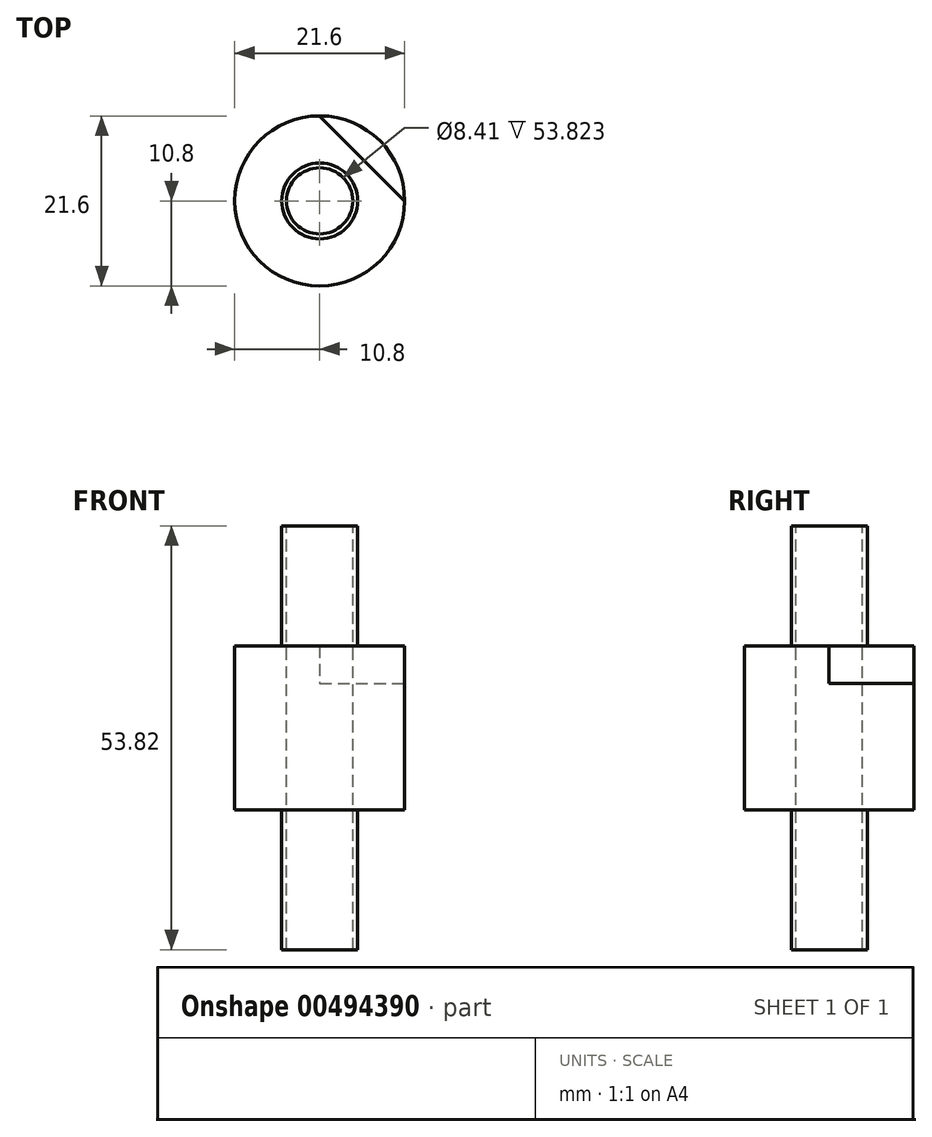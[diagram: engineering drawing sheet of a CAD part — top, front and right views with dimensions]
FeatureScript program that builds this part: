
annotation { "Feature Type Name" : "Feature", "Feature Type Description" : "" }
export const myFeature = defineFeature(function(context is Context, id is Id, definition is map)
    precondition{}
    {
        {
            var Q0;
            Q0=qCreatedBy(makeId("Front.planeOp"),FACE);
            var sketch = newSketch(context, id + "F0", { "sketchPlane" : qUnion([Q0])});
            skLineSegment(sketch, "E0", {"start": v(0, 19.99) * mm, "end": v(-4.83, 19.99) * mm});
            skLineSegment(sketch, "E1", {"start": v(-4.83, 19.99) * mm, "end": v(-4.83, 0) * mm});
            skLineSegment(sketch, "E2", {"start": v(-4.83, 0) * mm, "end": v(-10.8, 0) * mm});
            skLineSegment(sketch, "E3", {"start": v(-10.8, 0) * mm, "end": v(-10.8, -16.05) * mm});
            skLineSegment(sketch, "E4", {"start": v(-10.8, -16.05) * mm, "end": v(-4.83, -16.05) * mm});
            skLineSegment(sketch, "E5", {"start": v(-4.83, -16.05) * mm, "end": v(-4.83, -33.83) * mm});
            skLineSegment(sketch, "E6", {"start": v(-4.83, -33.83) * mm, "end": v(0, -33.83) * mm});
            skLineSegment(sketch, "E7", {"start": v(0, -33.83) * mm, "end": v(0, 19.99) * mm});
            skSolve(sketch);
        }
        {
            var Q0;
            Q0 = qSketchRegion(id + "F0", true);
            var Q1;
            Q1=sQuery(id+"F0.wireOp",EDGE,"E7");
            revolve(context, id + "F1", {"entities" : qUnion([Q0]), "axis" : qUnion([Q1]), "revolveType" : RevolveType.FULL});
        }
        {
            var Q0;
            Q0=makeQuery(id+"F1.opRevolve","SWEPT_FACE",FACE,{"disambiguationData":[OSD([sQuery(id+"F0.wireOp",EDGE,"E2")])]});
            var sketch = newSketch(context, id + "F2", { "sketchPlane" : qUnion([Q0])});
            skArc(sketch, "E8", {"start": v(0, 10.8) * mm, "mid": v(-7.63, -7.63) * mm, "end": v(10.8, 0) * mm});
            skLineSegment(sketch, "E9", {"start": v(0, 10.8) * mm, "end": v(10.8, 0) * mm});
            skSolve(sketch);
        }
        {
            var Q0;
            Q0 = qSketchRegion(id + "F2", true);
            extrude(context, id + "F3", {"entities" : qUnion([Q0]), "operationType" : NewBodyOperationType.ADD, "depth" : 4.75 * mm});
        }
        {
            var Q0;
            Q0=makeQuery(id+"F1.opRevolve","SWEPT_FACE",FACE,{"disambiguationData":[OSD([sQuery(id+"F0.wireOp",EDGE,"E0")])]});
            var sketch = newSketch(context, id + "F4", { "sketchPlane" : qUnion([Q0])});
            skCircle(sketch, "E10", {"center": v(0, 0) * mm, "radius": 4.2 * mm});
            skSolve(sketch);
        }
        {
            var Q0;
            Q0=sQuery(id+"F4.wireOp",VERTEX,"E10.center");
            var Q1;
            Q1=makeQuery(id+"F1.opRevolve","SWEPT_BODY",BODY,{"disambiguationData":[OSD([sQuery(id+"F0.wireOp",EDGE,"E0"),sQuery(id+"F0.wireOp",EDGE,"E1"),sQuery(id+"F0.wireOp",EDGE,"E2"),sQuery(id+"F0.wireOp",EDGE,"E3"),sQuery(id+"F0.wireOp",EDGE,"E4"),sQuery(id+"F0.wireOp",EDGE,"E5"),sQuery(id+"F0.wireOp",EDGE,"E6"),sQuery(id+"F0.wireOp",EDGE,"E7")])]});
            hole(context, id + "F5", {"style" : HoleStyle.SIMPLE, "endStyle" : HoleEndStyle.THROUGH, "holeDiameter" : 8.4 * mm, "isTappedThrough" : true, "tappedDepth" : 12.7 * mm, "tapClearance" : 3, "locations" : qUnion([Q0]), "scope" : qUnion([Q1])});
        }
    });
